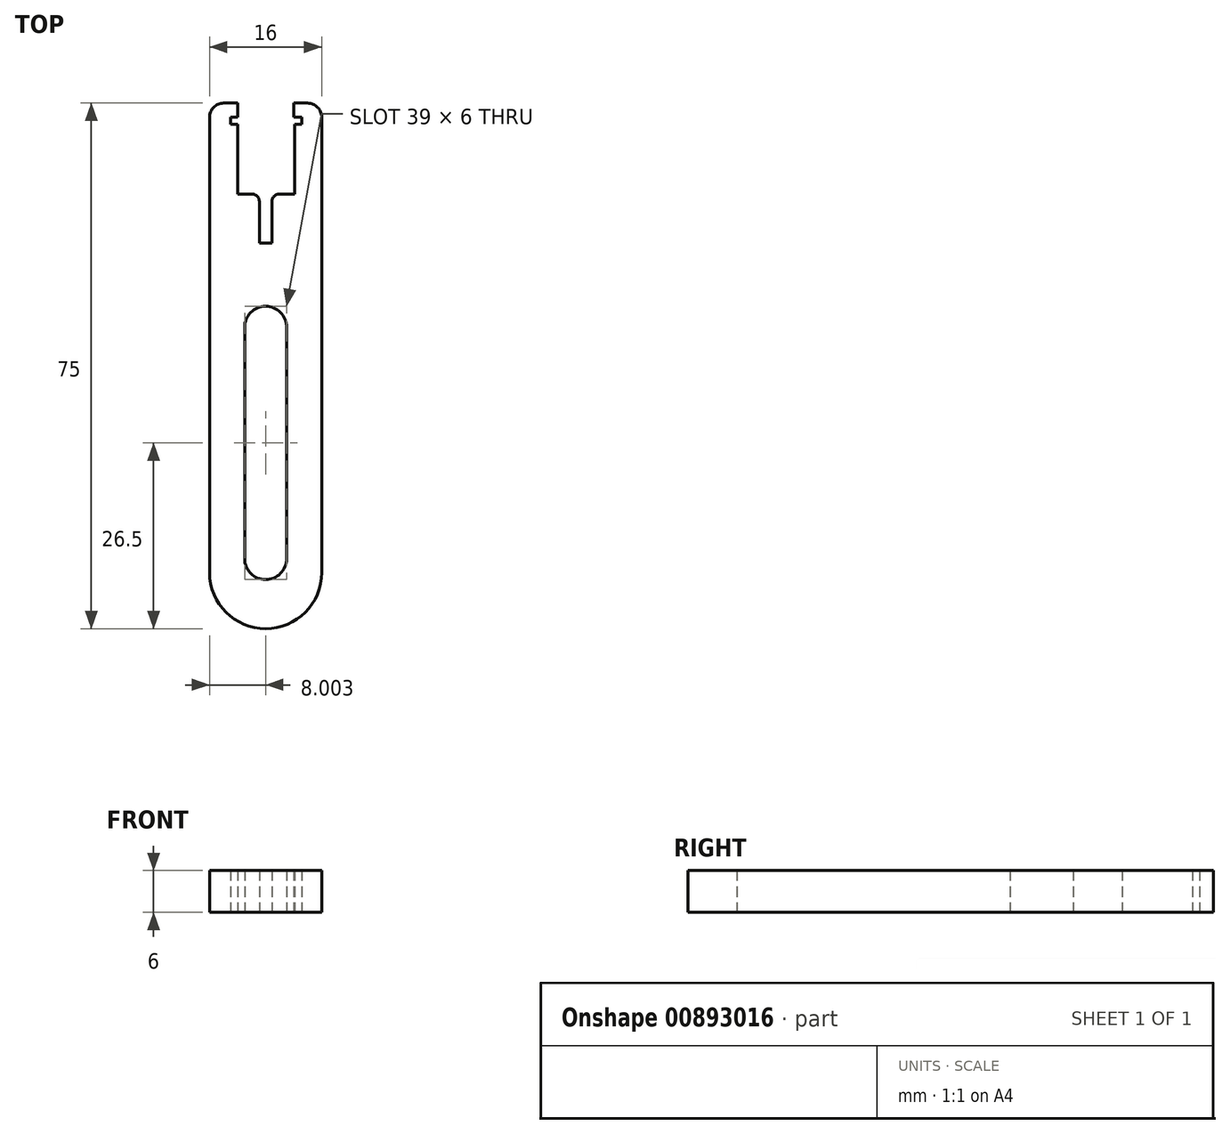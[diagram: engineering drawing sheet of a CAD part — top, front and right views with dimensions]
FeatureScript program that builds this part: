
annotation { "Feature Type Name" : "Feature", "Feature Type Description" : "" }
export const myFeature = defineFeature(function(context is Context, id is Id, definition is map)
    precondition{}
    {
        {
            var Q0;
            Q0=qCreatedBy(makeId("Top.planeOp"),FACE);
            var sketch = newSketch(context, id + "F0", { "sketchPlane" : qUnion([Q0])});
            skLineSegment(sketch, "E0.left", {"start": v(0.67, 63.67) * mm, "end": v(0.67, -1.33) * mm});
            skLineSegment(sketch, "E1", {"start": v(2.67, 65.67) * mm, "end": v(4.67, 65.67) * mm});
            skLineSegment(sketch, "E2", {"start": v(4.67, 52.67) * mm, "end": v(4.67, 62.67) * mm});
            skLineSegment(sketch, "E3.left", {"start": v(7.77, 51.67) * mm, "end": v(7.77, 45.67) * mm});
            skLineSegment(sketch, "E4", {"start": v(6.77, 52.67) * mm, "end": v(4.67, 52.67) * mm});
            skLineSegment(sketch, "E5", {"start": v(4.67, 63.67) * mm, "end": v(3.67, 63.67) * mm});
            skLineSegment(sketch, "E6", {"start": v(3.67, 63.67) * mm, "end": v(3.67, 62.67) * mm});
            skLineSegment(sketch, "E7", {"start": v(3.67, 62.67) * mm, "end": v(4.67, 62.67) * mm});
            skLineSegment(sketch, "E8.trimOffspring", {"start": v(4.67, 63.67) * mm, "end": v(4.67, 65.67) * mm});
            skLineSegment(sketch, "E9", {"start": v(8.67, -9.33) * mm, "end": v(8.67, -9.33) * mm});
            skPoint(sketch, "E10.visualSharp", {"position": v(0.67, 65.67) * mm});
            skArc(sketch, "E10.filletArc", {"start": v(2.67, 65.67) * mm, "mid": v(1.26, 65.08) * mm, "end": v(0.67, 63.67) * mm});
            skPoint(sketch, "E11.visualSharp", {"position": v(0.67, -9.33) * mm});
            skArc(sketch, "E11.filletArc", {"start": v(0.67, -1.33) * mm, "mid": v(3.02, -6.99) * mm, "end": v(8.67, -9.33) * mm});
            skLineSegment(sketch, "E12.MirrorCS", {"start": v(13.82, 62.67) * mm, "end": v(12.82, 62.67) * mm});
            skLineSegment(sketch, "E13.MirrorCS", {"start": v(13.82, 63.67) * mm, "end": v(13.82, 62.67) * mm});
            skLineSegment(sketch, "E14.MirrorCS", {"start": v(12.67, 63.67) * mm, "end": v(13.82, 63.67) * mm});
            skLineSegment(sketch, "E15.MirrorCS", {"start": v(12.67, 63.67) * mm, "end": v(12.67, 65.67) * mm});
            skArc(sketch, "E16.MirrorCS", {"start": v(14.67, 65.67) * mm, "mid": v(16.09, 65.08) * mm, "end": v(16.67, 63.67) * mm});
            skLineSegment(sketch, "E17.MirrorCS", {"start": v(10.57, 52.67) * mm, "end": v(12.82, 52.67) * mm});
            skLineSegment(sketch, "E18.MirrorCS", {"start": v(14.67, 65.67) * mm, "end": v(12.67, 65.67) * mm});
            skLineSegment(sketch, "E19.MirrorCS", {"start": v(9.57, 51.67) * mm, "end": v(9.57, 45.67) * mm});
            skPoint(sketch, "E20.MirrorP", {"position": v(16.67, 65.67) * mm});
            skLineSegment(sketch, "E21.MirrorCS", {"start": v(12.82, 52.67) * mm, "end": v(12.82, 62.67) * mm});
            skLineSegment(sketch, "E22", {"start": v(9.57, 45.67) * mm, "end": v(7.77, 45.67) * mm});
            skPoint(sketch, "E23.visualSharp", {"position": v(7.77, 52.67) * mm});
            skArc(sketch, "E23.filletArc", {"start": v(7.77, 51.67) * mm, "mid": v(7.48, 52.38) * mm, "end": v(6.77, 52.67) * mm});
            skPoint(sketch, "E24.visualSharp", {"position": v(9.57, 52.67) * mm});
            skArc(sketch, "E24.filletArc", {"start": v(10.57, 52.67) * mm, "mid": v(9.87, 52.38) * mm, "end": v(9.57, 51.67) * mm});
            skLineSegment(sketch, "E25", {"start": v(16.67, -1.33) * mm, "end": v(16.67, 63.67) * mm});
            skPoint(sketch, "E26.visualSharp", {"position": v(16.67, -9.33) * mm});
            skArc(sketch, "E26.filletArc", {"start": v(8.67, -9.33) * mm, "mid": v(14.33, -6.99) * mm, "end": v(16.67, -1.33) * mm});
            skLineSegment(sketch, "E27", {"start": v(11.67, 0.67) * mm, "end": v(11.67, 17.17) * mm});
            skLineSegment(sketch, "E28", {"start": v(5.67, 17.17) * mm, "end": v(5.67, 0.67) * mm});
            skLineSegment(sketch, "E29", {"start": v(8.67, -2.33) * mm, "end": v(8.67, -2.33) * mm});
            skPoint(sketch, "E30.visualSharp", {"position": v(5.67, -2.33) * mm});
            skArc(sketch, "E30.filletArc", {"start": v(5.67, 0.67) * mm, "mid": v(6.55, -1.45) * mm, "end": v(8.67, -2.33) * mm});
            skPoint(sketch, "E31.visualSharp", {"position": v(11.67, -2.33) * mm});
            skArc(sketch, "E31.filletArc", {"start": v(8.67, -2.33) * mm, "mid": v(10.8, -1.45) * mm, "end": v(11.67, 0.67) * mm});
            skPoint(sketch, "E32.MirrorP", {"position": v(11.67, 36.67) * mm});
            skArc(sketch, "E33.MirrorCS", {"start": v(8.67, 36.67) * mm, "mid": v(10.8, 35.8) * mm, "end": v(11.67, 33.67) * mm});
            skPoint(sketch, "E34.MirrorP", {"position": v(5.67, 36.67) * mm});
            skLineSegment(sketch, "E35.MirrorCS", {"start": v(5.67, 17.17) * mm, "end": v(5.67, 33.67) * mm});
            skLineSegment(sketch, "E36.MirrorCS", {"start": v(11.67, 33.67) * mm, "end": v(11.67, 17.17) * mm});
            skArc(sketch, "E37.MirrorCS", {"start": v(5.67, 33.67) * mm, "mid": v(6.55, 35.8) * mm, "end": v(8.67, 36.67) * mm});
            skSolve(sketch);
        }
        {
            var Q0;
            Q0=makeQuery(id+"F0.imprint","IMPRINT",FACE,{"disambiguationData":[TD([[makeQuery(id+"F0.imprint","IMPRINT",EDGE,{"derivedFrom":sQuery(id+"F0.wireOp",EDGE,"E0.left")}),1.0]])]});
            extrude(context, id + "F1", {"entities" : qUnion([Q0]), "depth" : 6 * mm, "offsetDistance" : 25 * mm});
        }
    });
